# Revit family: Sanitary_Basins_Ceramica-Globo_Classic-wall-hung-basin-SCQ80
name_source: partatom
category: Plumbing Fixtures
units: mm (PartAtom-declared; Revit-internal decimal feet)

## family parameters
Always vertical = Yes
Cut with Voids When Loaded = No
OmniClass Number = 23.45.00.00
OmniClass Title = Sanitary, Laundry, and Cleaning Equipment
Part Type = Normal
Room Calculation Point = No
Round Connector Dimension = Use Diameter
Shared = No
Work Plane-Based = No

## types (1)
- Default
    BIMobject category = Basins
    BIMobject category code = sanitary-basins
    BIMobject main category = Sanitary
    BIMobject main category code = sanitary
    BOSUseNativeGeometries = 1
    Brand url = http://www.ceramicaglobo.com
    Date of publishing = 7/19/2017
    Default Elevation = 0' - 0"
    Design country = Italy
    EAN code = https://8030963026214
    Edition number = 1
    IFC Classification = Sanitary Terminal
    Installation instructions = https://www.ceramicaglobo.com
    Manufacturer country = Italy
    Manufacturer name = Ceramica Globo
    Masterformat 2014 Code = 22 41 16.16
    Masterformat 2014 Description = Residential Sinks
    Material main = Fireclay
    Material secondary = Fireclay
    NBS Reference Code = 31-75
    NBS Reference Description = Sanitary Accessories
    OmniClass Code = 23-31 13 00
    OmniClass Description = Sinks
    Product Guid = faaa42f9-d0d8-4524-9973-70200728d304
    Product SKU = Classic-wall-hung-basin-SCQ80
    Product data url = https://bimobject.com
    Product family = Basins
    Product group = Classic
    Product name = Classic wall-hung basin SCQ80
    Product url = https://www.ceramicaglobo.com
    QR code = http://bimobject.com
    Technical description = https://www.ceramicaglobo.com
    UNSPSC Code = 301815
    Uniclass 2.0 Code = PR-31-75
    Uniclass 2.0 Description = Sanitary Accessories
    Uniclass 2015 Code = Pr_40_20_96_15
    Uniclass 2015 Name = Ceramic sinks
    Weight Net (Kg) = 26

## geometry (parser evidence)
native form markers: Sweep x5
no freeform markers — native parametric forms only
